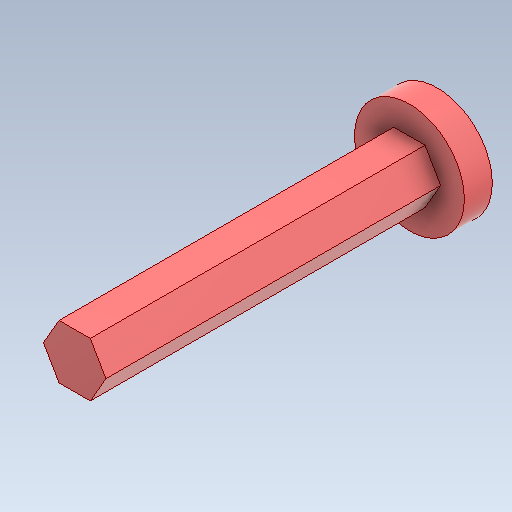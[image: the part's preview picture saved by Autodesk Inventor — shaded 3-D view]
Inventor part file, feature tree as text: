
AUTODESK INVENTOR PART (.ipt)
format: ipt  version: 2021.2 (Build 252289000, 289)  size: 123,392 bytes
history: native  units: in
note: dims shown in document units (in); Inventor stores cm internally (conversion verified against a paired STEP export)
features: extrude x2, other x2, sketch x2
ambient origin geometry x8: Origin, YZ Plane, XZ Plane, XY Plane, X Axis, Y Axis, Z Axis, Center Point
bodies: Solid1 (feature_tree)
feature tree (6):
  extrude  "Extrusion1"  Depth=3.0in TaperAngle=0.0deg
  extrude  "Extrusion2"  Depth=0.25in TaperAngle=0.0deg
  other  "Reduce Size of Hex Shaft"
  other  "Reduce Size of Bushing"
  sketch  "Sketch1"  dims[d0=0.5in d1=3.0in d2=0.0in]
  sketch  "Sketch2"  dims[d3=1.0in d4=0.25in d5=0.0in d6=0.0075in d7=0.005in d8=0.0075in d9=0.01in]
